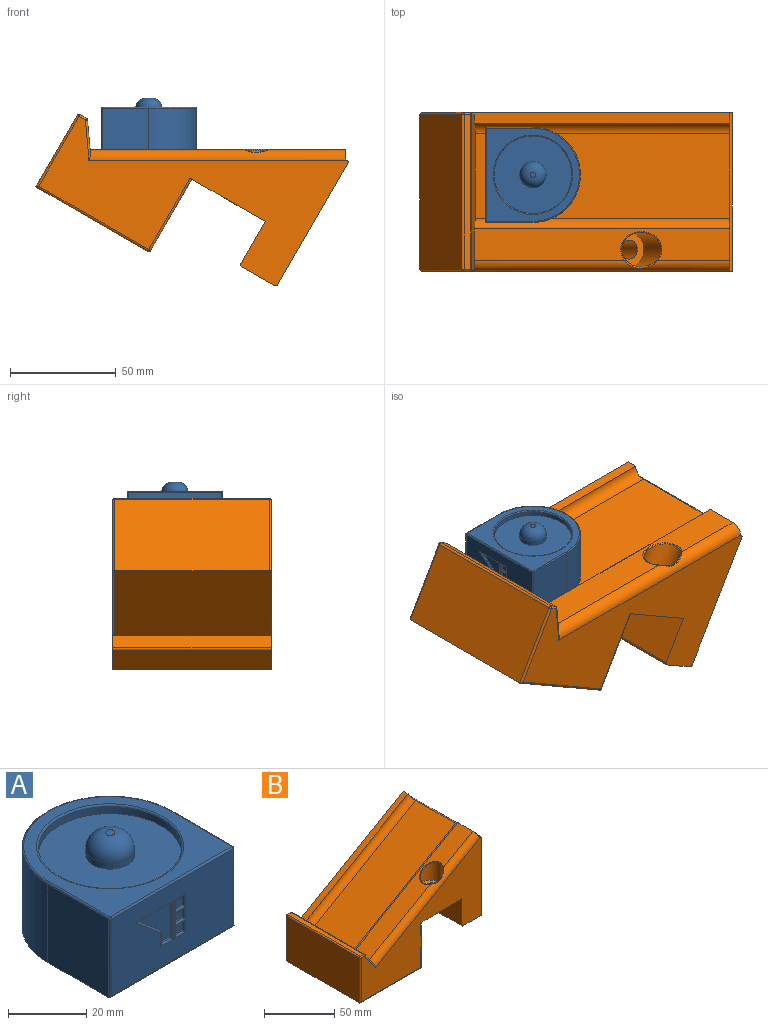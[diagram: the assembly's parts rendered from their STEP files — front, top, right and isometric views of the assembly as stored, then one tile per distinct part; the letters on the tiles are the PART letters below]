
ASSEMBLY  parts=2 mates=1
PART A: 60 faces, bbox 48.7x46.9x29.3 mm
  f0: plane 44x24mm, normal (0,-1,0), area 918.2mm2, adj f34,f36,f38,f39,f44,f45,f46,f48
  f1: cylinder r=22.5mm len=45mm, axis (0,0,-1), area 1731.8mm2, adj f2,f4,f6,f40
  f2: plane 24.5x22mm, normal (-1,0,0), area 539mm2, adj f1,f6,f39,f42
  f3: cylinder r=18.3mm len=36.6mm, axis (0,0,-1), area 253mm2, adj f7,f59
  f4: plane 24.5x22mm, normal (1,0,0), area 539mm2, adj f1,f6,f34,f37
  f5: plane 44x44mm, normal (0,0,1), area 617.9mm2, adj f37,f38,f40,f42,f59
  f6: plane 45x44.5mm, normal (0,0,-1), area 1546.8mm2, adj f1,f2,f4,f36,f43
  f7: plane 36.6x36.6mm, normal (0,0,1), area 929.4mm2, adj f3,f30
  f8: plane 3x0.5mm, normal (0,0,-1), area 1.5mm2, adj f9,f11,f12,f50
  f9: plane 3x0.5mm, normal (1,0,0), area 1.5mm2, adj f8,f10,f12,f51
  f10: plane 3x0.5mm, normal (0,0,1), area 1.5mm2, adj f9,f11,f12,f53
  f11: plane 3x0.5mm, normal (-1,0,0), area 1.5mm2, adj f8,f10,f12,f52
  f12: plane 3x3mm, normal (0,-1,0), area 9mm2, adj f8,f9,f10,f11
  f13: plane 3x0.5mm, normal (0,0,-1), area 1.5mm2, adj f14,f16,f17,f47
  f14: plane 3x0.5mm, normal (1,0,0), area 1.5mm2, adj f13,f15,f17,f48
  f15: plane 3x0.5mm, normal (0,0,1), area 1.5mm2, adj f14,f16,f17,f50
  f16: plane 3x0.5mm, normal (-1,0,0), area 1.5mm2, adj f13,f15,f17,f49
  f17: plane 3x3mm, normal (0,-1,0), area 9mm2, adj f13,f14,f15,f16
  f18: plane 3x0.5mm, normal (0,0,-1), area 1.5mm2, adj f19,f21,f22,f44
  f19: plane 3x0.5mm, normal (1,0,0), area 1.5mm2, adj f18,f20,f22,f45
  f20: plane 3x0.5mm, normal (0,0,1), area 1.5mm2, adj f19,f21,f22,f47
  f21: plane 3x0.5mm, normal (-1,0,0), area 1.5mm2, adj f18,f20,f22,f46
  f22: plane 3x3mm, normal (0,-1,0), area 9mm2, adj f18,f19,f20,f21
  f23: plane 11.86x0.5mm, normal (0,0,-1), area 5.9mm2, adj f24,f27,f28,f55
  f24: plane 8.34x7mm, normal (0.64,0,0.77), area 5.4mm2, adj f23,f25,f28,f54
  f25: plane 4x0.5mm, normal (1,0,0), area 2mm2, adj f24,f26,f28,f56
  f26: plane 3.52x0.5mm, normal (0,0,1), area 1.8mm2, adj f25,f27,f28,f58
  f27: plane 11x0.5mm, normal (-1,0,0), area 5.5mm2, adj f23,f26,f28,f57
  f28: plane 11.86x11mm, normal (0,-1,0), area 67.9mm2, adj f23,f24,f25,f26,f27
  f29: plane 6.47x6.47mm, normal (0,0,-1), area 32.8mm2, adj f33
  f30: cylinder r=6.25mm len=12.5mm, axis (0,0,-1), area 78.5mm2, adj f7,f32
  f31: plane 2.5x2.5mm, normal (0,0,1), area 4.9mm2, adj f32
  f32: torus R=1.25mm, axis (0,0,1), area 218.8mm2, adj f30,f31
  f33: torus R=3.23mm, axis (0,0,-1), area 293.1mm2, adj f29,f43
  f34: cylinder r=0.5mm len=24.5mm, axis (0,0,1), area 19.1mm2, adj f0,f4,f35,f36
  f35: sphere r=0.5mm, area 0.4mm2, adj f34,f37,f38
  f36: cylinder r=0.5mm len=45mm, axis (1,0,0), area 35.1mm2, adj f0,f6,f34,f39
  f37: cylinder r=0.5mm len=22mm, axis (0,-1,0), area 17.3mm2, adj f4,f5,f35,f40
  f38: cylinder r=0.5mm len=44mm, axis (-1,0,0), area 34.6mm2, adj f0,f5,f35,f41
  f39: cylinder r=0.5mm len=24.5mm, axis (0,0,-1), area 19.1mm2, adj f0,f2,f36,f41
  f40: torus R=22mm, axis (0,0,1), area 55.1mm2, adj f1,f5,f37,f42
  f41: sphere r=0.5mm, area 0.4mm2, adj f38,f39,f42
  f42: cylinder r=0.5mm len=22mm, axis (0,1,0), area 17.3mm2, adj f2,f5,f40,f41
  f43: torus R=8.71mm, axis (0,0,1), area 39.1mm2, adj f6,f33
  f44: cylinder r=0.5mm len=4mm, axis (-1,0,0), area 2.6mm2, adj f0,f18,f45,f46
  f45: cylinder r=0.5mm len=4mm, axis (0,0,-1), area 2.6mm2, adj f0,f19,f44,f47
  f46: cylinder r=0.5mm len=4mm, axis (0,0,1), area 2.6mm2, adj f0,f21,f44,f47
  f47: cylinder r=0.5mm len=4mm, axis (1,0,0), area 5.3mm2, adj f13,f20,f45,f46,f48,f49
  f48: cylinder r=0.5mm len=4mm, axis (0,0,-1), area 2.6mm2, adj f0,f14,f47,f50
  f49: cylinder r=0.5mm len=4mm, axis (0,0,1), area 2.6mm2, adj f0,f16,f47,f50
  f50: cylinder r=0.5mm len=4mm, axis (1,0,0), area 5.3mm2, adj f8,f15,f48,f49,f51,f52
  f51: cylinder r=0.5mm len=4mm, axis (0,0,-1), area 2.6mm2, adj f0,f9,f50,f53
  f52: cylinder r=0.5mm len=4mm, axis (0,0,1), area 2.6mm2, adj f0,f11,f50,f53
  f53: cylinder r=0.5mm len=4mm, axis (1,0,0), area 2.6mm2, adj f0,f10,f51,f52
  f54: cylinder r=0.5mm len=9.72mm, axis (0.77,0,-0.64), area 8.9mm2, adj f0,f24,f55,f56
  f55: cylinder r=0.5mm len=13.73mm, axis (-1,0,0), area 9.8mm2, adj f0,f23,f54,f57
  f56: cylinder r=0.5mm len=4.5mm, axis (0,0,-1), area 3.2mm2, adj f0,f25,f54,f58
  f57: cylinder r=0.5mm len=12mm, axis (0,0,1), area 8.9mm2, adj f0,f27,f55,f58
  f58: cylinder r=0.5mm len=4.52mm, axis (1,0,0), area 3mm2, adj f0,f26,f56,f57
  f59: torus R=18.8mm, axis (0,0,1), area 91.2mm2, adj f3,f5
PART B: 46 faces, bbox 122.2x75.2x88.7 mm
  f0: cylinder r=5mm len=107.65mm, axis (-0.87,0,-0.5), area 907.8mm2, adj f1,f17,f21,f22,f41,f45
  f1: plane 73.18x15.76mm, normal (0.82,0,0.57), area 1264.1mm2, adj f0,f2,f9,f20,f22,f24,f25,f33
  f2: plane 104.28x60.21mm, normal (-0.5,0,0.87), area 4816.7mm2, adj f1,f8,f24,f25
  f3: plane 75x23mm, normal (-1,0,0), area 1725mm2, adj f4,f16,f17,f18
  f4: cylinder r=1mm len=75mm, axis (0,1,0), area 117.8mm2, adj f3,f5,f17,f18
  f5: plane 75x18mm, normal (0,0,-1), area 1350mm2, adj f4,f6,f17,f18
  f6: cylinder r=1mm len=75mm, axis (0,1,0), area 117.8mm2, adj f5,f7,f17,f18
  f7: plane 75x66.34mm, normal (1,0,0), area 4975.7mm2, adj f6,f8,f17,f18
  f8: cylinder r=1mm len=75mm, axis (0,1,0), area 157.1mm2, adj f2,f7,f17,f18,f19,f21
  f9: cylinder r=1mm len=73mm, axis (0,1,0), area 70.1mm2, adj f1,f10,f32,f40
  f10: plane 73x3.48mm, normal (0,0,1), area 254mm2, adj f9,f11,f31,f39
  f11: cylinder r=1mm len=73mm, axis (0,1,0), area 114.7mm2, adj f10,f12,f30,f38
  f12: plane 73x39mm, normal (-1,0,0), area 2847mm2, adj f11,f13,f29,f37
  f13: plane 73x60.89mm, normal (0,0,-1), area 4444.8mm2, adj f12,f14,f28,f36
  f14: cylinder r=1mm len=73mm, axis (0,1,0), area 114.7mm2, adj f13,f15,f27,f35
  f15: plane 73x39mm, normal (1,0,0), area 2847mm2, adj f14,f16,f26,f34
  f16: plane 75x41.1mm, normal (0,0,-1), area 2944.3mm2, adj f3,f15,f17,f18,f23,f26,f34
  f17: plane 120.99x83.34mm, normal (0,-1,0), area 4239.7mm2, adj f0,f3,f4,f5,f6,f7,f8,f16
  f18: plane 120.99x87.54mm, normal (0,1,0), area 4847.9mm2, adj f3,f4,f5,f6,f7,f8,f16,f19
  f19: plane 10x4.33mm, normal (0.87,0,0.5), area 30.4mm2, adj f8,f18,f20,f24
  f20: plane 105.57x60.97mm, normal (-0.5,0,0.87), area 604.5mm2, adj f1,f18,f19,f24,f33
  f21: plane 25x4.33mm, normal (0.87,0,0.5), area 100mm2, adj f0,f8,f22,f25
  f22: plane 104.66x60.43mm, normal (-0.5,0,0.87), area 1585.2mm2, adj f0,f1,f21,f25,f44
  f23: cylinder r=4.5mm len=15.7mm, axis (0,0,-1), area 443.9mm2, adj f16,f42
  f24: cylinder r=5mm len=107.16mm, axis (-0.87,0,-0.5), area 947.5mm2, adj f1,f2,f19,f20
  f25: cylinder r=5mm len=107.16mm, axis (0.87,0,0.5), area 947.5mm2, adj f1,f2,f21,f22
  f26: cylinder r=1mm len=39mm, axis (0,0,1), area 61.3mm2, adj f15,f16,f18,f27
  f27: sphere r=1mm, area 1.6mm2, adj f14,f26,f28
  f28: cylinder r=1mm len=60.89mm, axis (1,0,0), area 95.1mm2, adj f13,f18,f27,f29
  f29: cylinder r=1mm len=39mm, axis (0,0,-1), area 60.7mm2, adj f12,f18,f28,f30
  f30: sphere r=1mm, area 1.6mm2, adj f11,f29,f31
  f31: cylinder r=1mm len=3.48mm, axis (-1,0,0), area 5.5mm2, adj f10,f18,f30,f32
  f32: sphere r=1mm, area 1mm2, adj f9,f31,f33
  f33: cylinder r=1mm len=12.04mm, axis (-0.57,0,0.82), area 21.9mm2, adj f1,f18,f20,f32
  f34: cylinder r=1mm len=39mm, axis (0,0,-1), area 61.3mm2, adj f15,f16,f17,f35
  f35: sphere r=1mm, area 1.6mm2, adj f14,f34,f36
  f36: cylinder r=1mm len=60.89mm, axis (-1,0,0), area 95.1mm2, adj f13,f17,f35,f37
  f37: cylinder r=1mm len=39mm, axis (0,0,1), area 60.7mm2, adj f12,f17,f36,f38
  f38: sphere r=1mm, area 1.6mm2, adj f11,f37,f39
  f39: cylinder r=1mm len=3.48mm, axis (1,0,0), area 5.5mm2, adj f10,f17,f38,f40
  f40: sphere r=1mm, area 1mm2, adj f9,f39,f41
  f41: cylinder r=1mm len=16.08mm, axis (0.57,0,-0.82), area 27.4mm2, adj f0,f1,f17,f40
  f42: plane 16x16mm, normal (0,0,1), area 137.4mm2, adj f23,f43
  f43: cylinder r=8mm len=16.38mm, axis (0,0,1), area 564.2mm2, adj f42,f44,f45
  f44: bspline ~16.99x13.77mm, area 30.6mm2, adj f22,f43,f45
  f45: bspline ~14.53x8.94mm, area 17.3mm2, adj f0,f43,f44
PLACE A rot(axis=(0,0,-1),90deg) t=(-41.27,-49.25,-153.47)mm
PLACE B rot(axis=(0,1,0),30deg) t=(-115.49,-19.82,-126.4)mm
MATE planar A.f6 <-> B.f2  axis (0,0,-1) through (-41.27,-26.75,-153.47)mm
